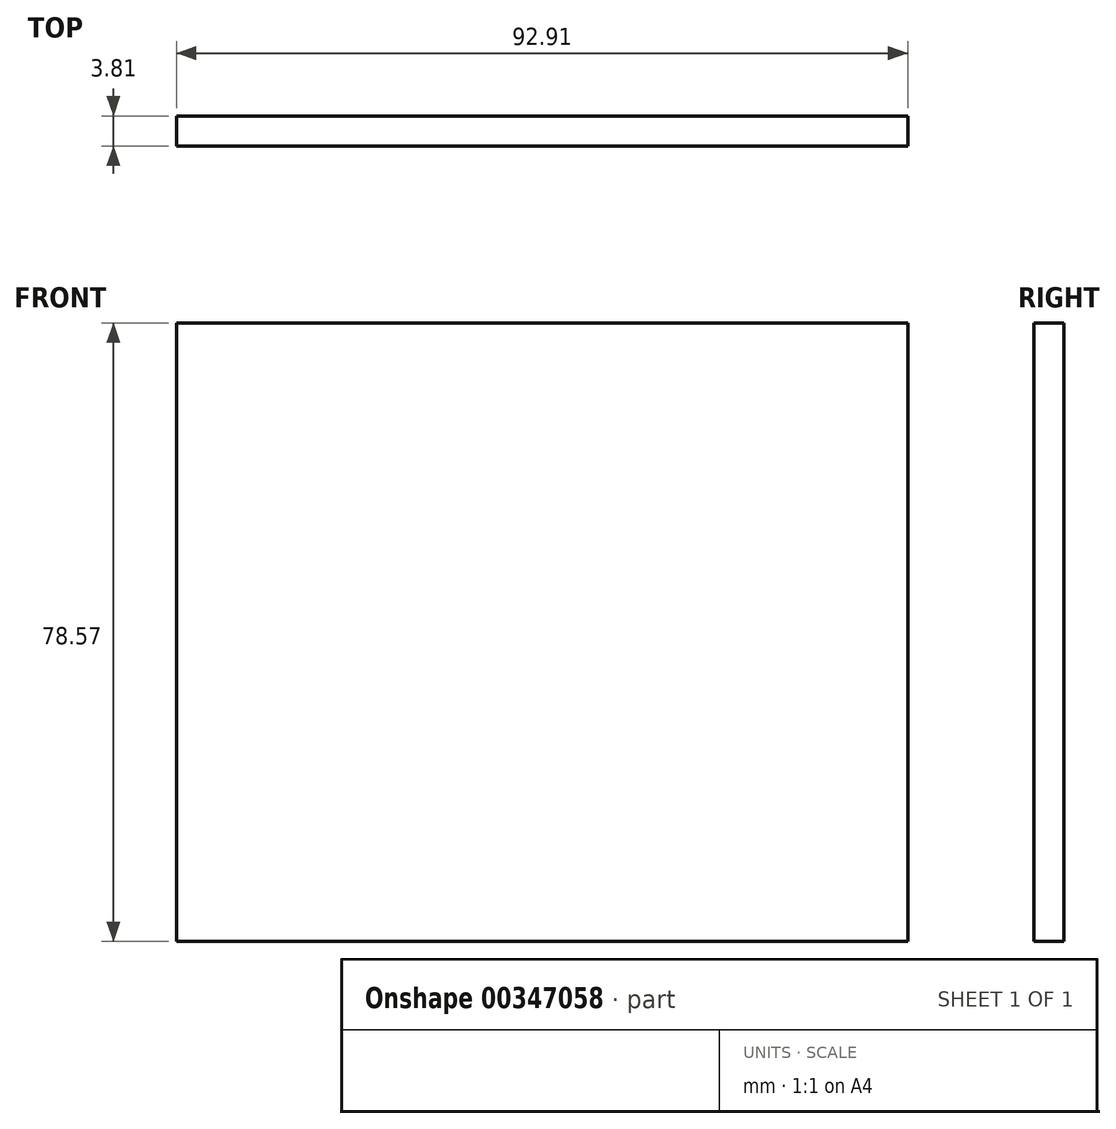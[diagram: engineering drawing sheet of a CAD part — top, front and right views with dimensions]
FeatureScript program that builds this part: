
annotation { "Feature Type Name" : "Feature", "Feature Type Description" : "" }
export const myFeature = defineFeature(function(context is Context, id is Id, definition is map)
    precondition{}
    {
        {
            var Q0;
            Q0=qCreatedBy(makeId("Front.planeOp"),FACE);
            var sketch = newSketch(context, id + "F0", { "sketchPlane" : qUnion([Q0])});
            skLineSegment(sketch, "E0.bottom", {"start": v(-55.73, 38.43) * mm, "end": v(37.18, 38.43) * mm});
            skLineSegment(sketch, "E0.top", {"start": v(-55.73, -40.14) * mm, "end": v(37.18, -40.14) * mm});
            skLineSegment(sketch, "E0.left", {"start": v(-55.73, 38.43) * mm, "end": v(-55.73, -40.14) * mm});
            skLineSegment(sketch, "E0.right", {"start": v(37.18, 38.43) * mm, "end": v(37.18, -40.14) * mm});
            skSolve(sketch);
        }
        {
            var Q0;
            Q0=makeQuery(id+"F0.imprint","IMPRINT",FACE,{"disambiguationData":[TD([[makeQuery(id+"F0.imprint","IMPRINT",EDGE,{"derivedFrom":sQuery(id+"F0.wireOp",EDGE,"E0.bottom")}),-1.0]])]});
            extrude(context, id + "F1", {"entities" : qUnion([Q0]), "depth" : 3.8 * mm});
        }
        {
            var Q0;
            Q0=makeQuery(id+"F1.opExtrude","CAP_FACE",FACE,{"disambiguationData":[OSD([sQuery(id+"F0.wireOp",EDGE,"E0.bottom"),sQuery(id+"F0.wireOp",EDGE,"E0.top"),sQuery(id+"F0.wireOp",EDGE,"E0.left"),sQuery(id+"F0.wireOp",EDGE,"E0.right")])],"isStart":true});
            var sketch = newSketch(context, id + "F2", { "sketchPlane" : qUnion([Q0])});
            skFitSpline(sketch, "E1", {"points": [v(0, -9.64) * mm, v(25.3, 0) * mm, v(0, 19.78) * mm, v(31.35, 23.99) * mm], "startDerivative": vector(130.22, 20.76) * mm, "endDerivative": vector(146.74, -1.57) * mm});
            skSolve(sketch);
        }
        {
            var Q0;
            Q0 = qSketchRegion(id + "F2", true);
            var Q1;
            Q1=sQuery(id+"F2.wireOp",EDGE,"E1");
            extrude(context, id + "F3", {"entities" : qUnion([Q0]), "bodyType" : ToolBodyType.SURFACE, "surfaceEntities" : qUnion([Q1]), "oppositeDirection" : true, "depth" : 18.56 * mm});
        }
    });
